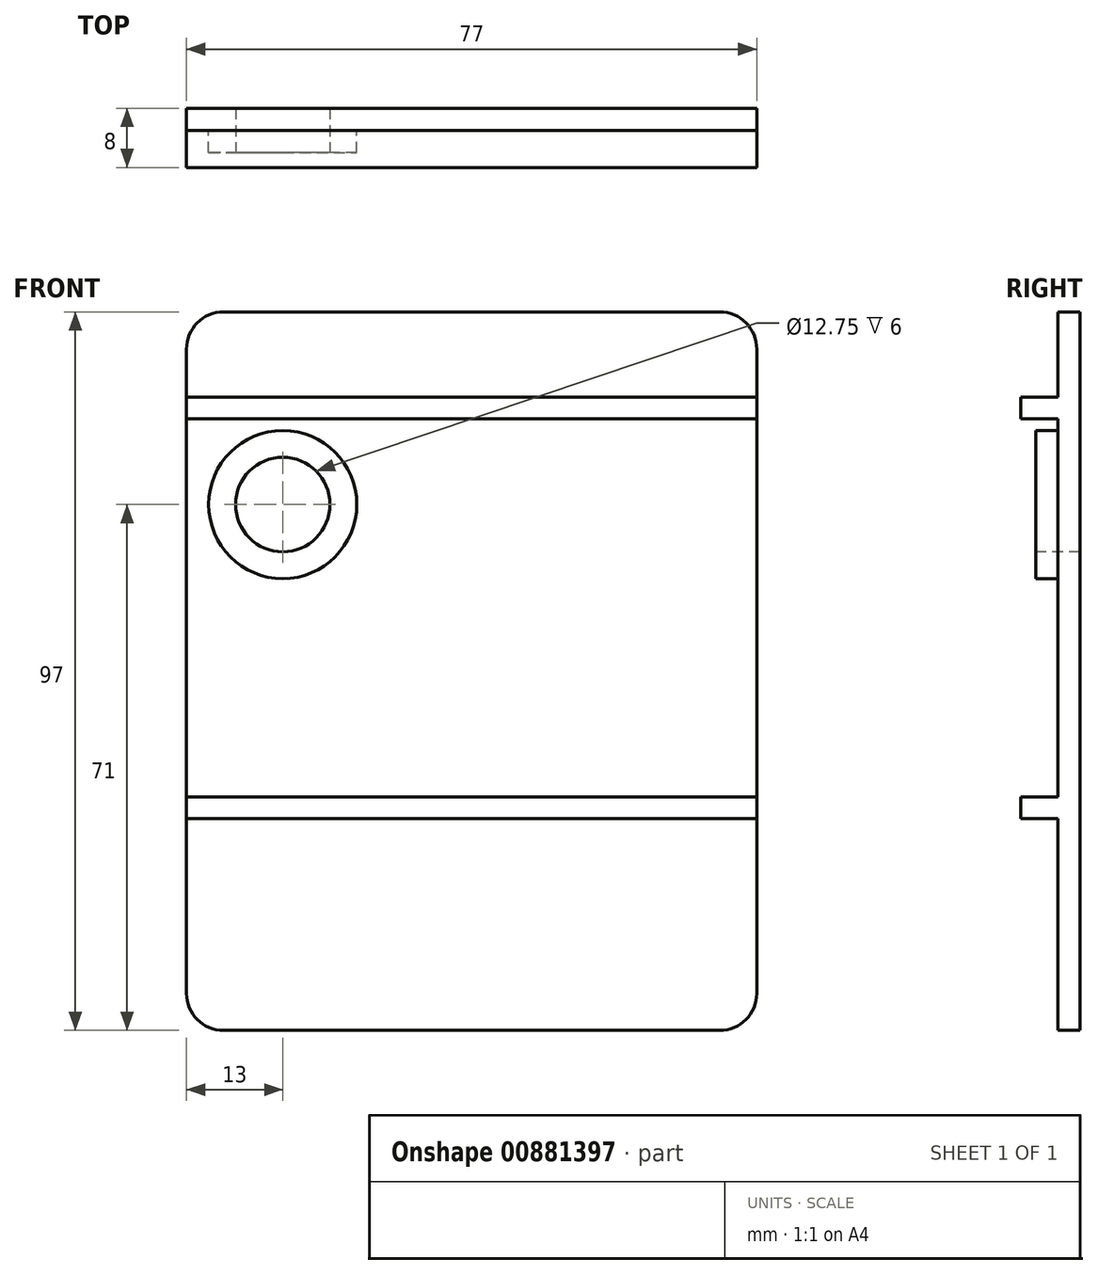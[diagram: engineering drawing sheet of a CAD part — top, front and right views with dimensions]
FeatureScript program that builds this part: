
annotation { "Feature Type Name" : "Feature", "Feature Type Description" : "" }
export const myFeature = defineFeature(function(context is Context, id is Id, definition is map)
    precondition{}
    {
        {
            var Q0;
            Q0=qCreatedBy(makeId("Front.planeOp"),FACE);
            var sketch = newSketch(context, id + "F0", { "sketchPlane" : qUnion([Q0])});
            skLineSegment(sketch, "E0.bottom", {"start": v(38.5, -48.5) * mm, "end": v(-38.5, -48.5) * mm});
            skLineSegment(sketch, "E0.top", {"start": v(38.5, 48.5) * mm, "end": v(-38.5, 48.5) * mm});
            skLineSegment(sketch, "E0.left", {"start": v(38.5, -48.5) * mm, "end": v(38.5, 48.5) * mm});
            skLineSegment(sketch, "E0.right", {"start": v(-38.5, -48.5) * mm, "end": v(-38.5, 48.5) * mm});
            skPoint(sketch, "E0.middle", {"position": v(0, 0) * mm});
            skPoint(sketch, "E1", {"position": v(-25.5, 22.5) * mm});
            skCircle(sketch, "E2", {"center": v(-25.5, 22.5) * mm, "radius": 6.38 * mm});
            skSolve(sketch);
        }
        {
            var Q0;
            Q0=makeQuery(id+"F0.imprint","IMPRINT",FACE,{"disambiguationData":[TD([[makeQuery(id+"F0.imprint","IMPRINT",EDGE,{"derivedFrom":sQuery(id+"F0.wireOp",EDGE,"E0.bottom")}),-1.0]])]});
            extrude(context, id + "F1", {"entities" : qUnion([Q0]), "oppositeDirection" : true, "depth" : 3 * mm});
        }
        {
            var Q0;
            Q0=makeQuery(id+"F1.opExtrude","CAP_FACE",FACE,{"disambiguationData":[OSD([sQuery(id+"F0.wireOp",EDGE,"E0.bottom"),sQuery(id+"F0.wireOp",EDGE,"E0.top"),sQuery(id+"F0.wireOp",EDGE,"E0.left"),sQuery(id+"F0.wireOp",EDGE,"E0.right"),sQuery(id+"F0.wireOp",EDGE,"E2")])],"isStart":true});
            var sketch = newSketch(context, id + "F2", { "sketchPlane" : qUnion([Q0])});
            skPoint(sketch, "E3", {"position": v(-25.5, 22.5) * mm});
            skCircle(sketch, "E4", {"center": v(-25.5, 22.5) * mm, "radius": 10 * mm});
            skCircle(sketch, "E5", {"center": v(-25.5, 22.5) * mm, "radius": 6.38 * mm});
            skSolve(sketch);
        }
        {
            var Q0;
            Q0=makeQuery(id+"F2.imprint","IMPRINT",FACE,{"disambiguationData":[TD([[makeQuery(id+"F2.imprint","IMPRINT",EDGE,{"derivedFrom":sQuery(id+"F2.wireOp",EDGE,"E4")}),1.0]])]});
            extrude(context, id + "F3", {"entities" : qUnion([Q0]), "operationType" : NewBodyOperationType.ADD, "depth" : 3 * mm});
        }
        {
            var Q0;
            Q0=makeQuery(id+"F1.opExtrude","CAP_FACE",FACE,{"disambiguationData":[OSD([sQuery(id+"F0.wireOp",EDGE,"E0.bottom"),sQuery(id+"F0.wireOp",EDGE,"E0.top"),sQuery(id+"F0.wireOp",EDGE,"E0.left"),sQuery(id+"F0.wireOp",EDGE,"E0.right"),sQuery(id+"F0.wireOp",EDGE,"E2")])],"isStart":true});
            var sketch = newSketch(context, id + "F4", { "sketchPlane" : qUnion([Q0])});
            skLineSegment(sketch, "E6.left", {"start": v(-38.5, 35.7) * mm, "end": v(-38.5, 34.1) * mm});
            skLineSegment(sketch, "E6.right", {"start": v(38.5, 35.7) * mm, "end": v(38.5, 34.1) * mm});
            skPoint(sketch, "E7", {"position": v(-38.5, -16.9) * mm});
            skPoint(sketch, "E8", {"position": v(-38.5, 34.1) * mm});
            skPoint(sketch, "E9", {"position": v(-38.5, 37.1) * mm});
            skPoint(sketch, "E10", {"position": v(-38.5, -19.9) * mm});
            skLineSegment(sketch, "E11.bottom", {"start": v(-38.5, 34.1) * mm, "end": v(38.5, 34.1) * mm});
            skLineSegment(sketch, "E11.top", {"start": v(-38.5, 37) * mm, "end": v(38.5, 37) * mm});
            skLineSegment(sketch, "E11.left", {"start": v(-38.5, 34.1) * mm, "end": v(-38.5, 37) * mm});
            skLineSegment(sketch, "E11.right", {"start": v(38.5, 34.1) * mm, "end": v(38.5, 37) * mm});
            skLineSegment(sketch, "E12.bottom", {"start": v(-38.5, -19.9) * mm, "end": v(38.5, -19.9) * mm});
            skLineSegment(sketch, "E12.top", {"start": v(-38.5, -16.97) * mm, "end": v(38.5, -16.97) * mm});
            skLineSegment(sketch, "E12.left", {"start": v(-38.5, -19.9) * mm, "end": v(-38.5, -16.97) * mm});
            skLineSegment(sketch, "E12.right", {"start": v(38.5, -19.9) * mm, "end": v(38.5, -16.97) * mm});
            skSolve(sketch);
        }
        {
            var Q0;
            {var subQ0=sQuery(id+"F4.wireOp",EDGE,"E11.bottom");Q0=makeQuery(id+"F4.imprint","IMPRINT",FACE,{"disambiguationData":[TD([[makeQuery(id+"F4.imprint","IMPRINT",EDGE,{"derivedFrom":subQ0}),1.0]])]});}
            var Q1;
            Q1=makeQuery(id+"F4.imprint","IMPRINT",FACE,{"disambiguationData":[TD([[makeQuery(id+"F4.imprint","IMPRINT",EDGE,{"derivedFrom":sQuery(id+"F4.wireOp",EDGE,"E12.bottom")}),1.0]])]});
            extrude(context, id + "F5", {"entities" : qUnion([Q0, Q1]), "operationType" : NewBodyOperationType.ADD, "depth" : 5 * mm});
        }
        {
            var Q0;
            Q0=makeQuery(id+"F1.opExtrude","SWEPT_EDGE",EDGE,{"disambiguationData":[OSD([sQuery(id+"F0.wireOp",EDGE,"E0.top"),sQuery(id+"F0.wireOp",EDGE,"E0.left")])]});
            var Q1;
            Q1=makeQuery(id+"F1.opExtrude","SWEPT_EDGE",EDGE,{"disambiguationData":[OSD([sQuery(id+"F0.wireOp",EDGE,"E0.top"),sQuery(id+"F0.wireOp",EDGE,"E0.right")])]});
            var Q2;
            Q2=makeQuery(id+"F1.opExtrude","SWEPT_EDGE",EDGE,{"disambiguationData":[OSD([sQuery(id+"F0.wireOp",EDGE,"E0.bottom"),sQuery(id+"F0.wireOp",EDGE,"E0.left")])]});
            var Q3;
            Q3=makeQuery(id+"F1.opExtrude","SWEPT_EDGE",EDGE,{"disambiguationData":[OSD([sQuery(id+"F0.wireOp",EDGE,"E0.bottom"),sQuery(id+"F0.wireOp",EDGE,"E0.right")])]});
            fillet(context, id + "F6", {"entities" : qUnion([Q0, Q1, Q2, Q3]), "radius" : 5 * mm, "tangentPropagation" : true, "allowEdgeOverflow" : false});
        }
    });
